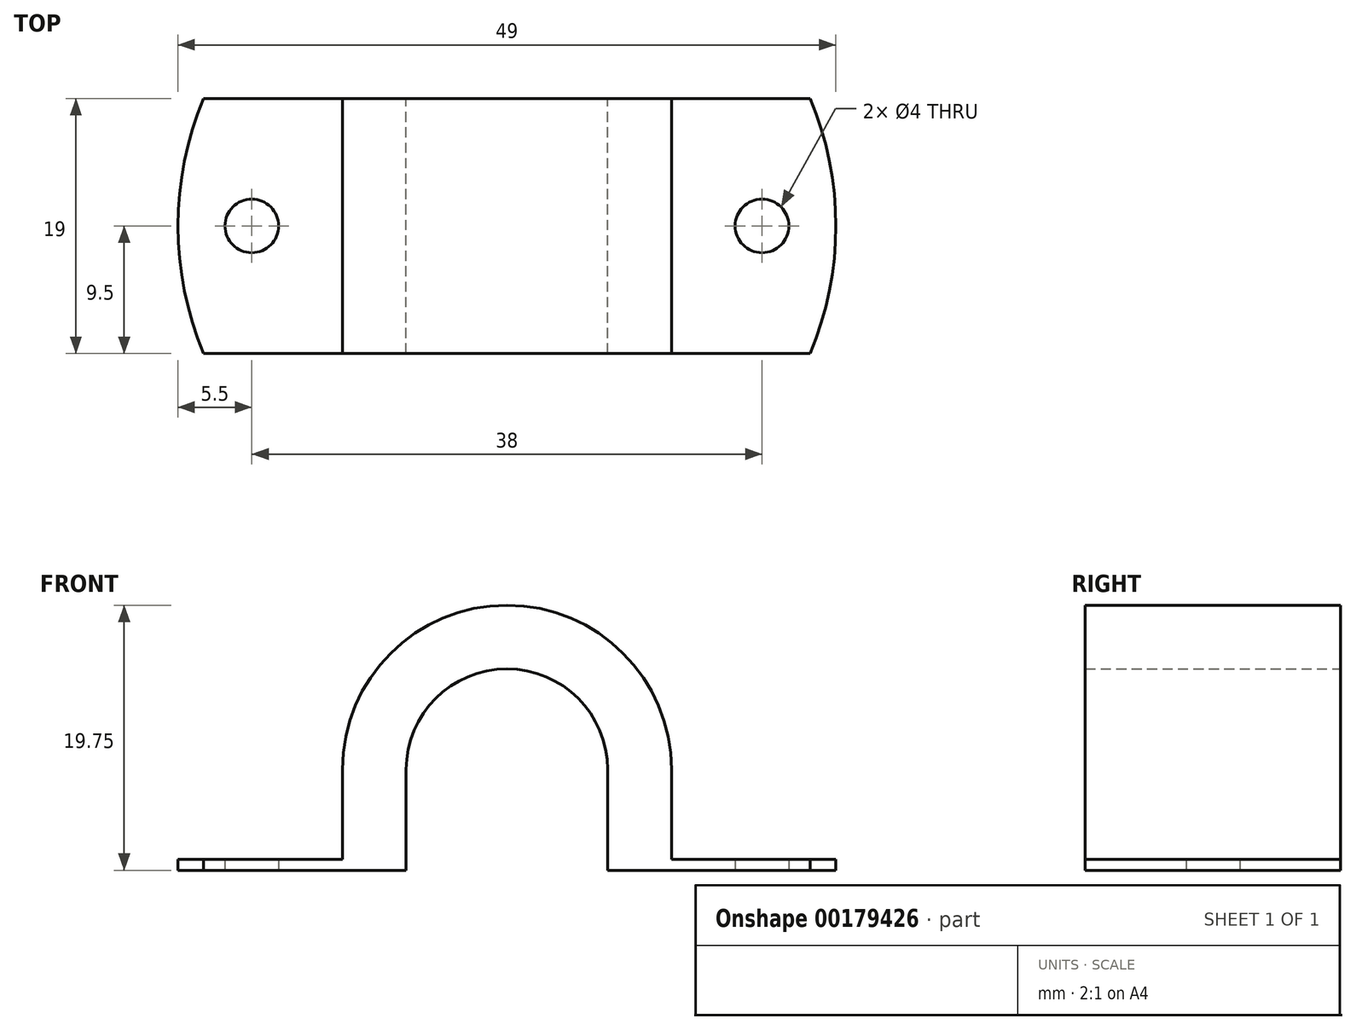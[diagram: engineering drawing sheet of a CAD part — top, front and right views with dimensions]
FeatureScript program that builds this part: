
annotation { "Feature Type Name" : "Feature", "Feature Type Description" : "" }
export const myFeature = defineFeature(function(context is Context, id is Id, definition is map)
    precondition{}
    {
        {
            var Q0;
            Q0=qCreatedBy(makeId("Front.planeOp"),FACE);
            var sketch = newSketch(context, id + "F0", { "sketchPlane" : qUnion([Q0])});
            skLineSegment(sketch, "E0", {"start": v(0, 21.46) * mm, "end": v(0, -15.22) * mm, "construction": true});
            skArc(sketch, "E1", {"start": v(7.5, 7.5) * mm, "mid": v(0, 15) * mm, "end": v(-7.5, 7.5) * mm});
            skLineSegment(sketch, "E2", {"start": v(-24.5, 0) * mm, "end": v(-7.5, 0) * mm});
            skArc(sketch, "E3", {"start": v(12.25, 7.5) * mm, "mid": v(0, 19.75) * mm, "end": v(-12.25, 7.5) * mm});
            skLineSegment(sketch, "E4", {"start": v(-12.25, 7.5) * mm, "end": v(-12.25, 0.8) * mm});
            skLineSegment(sketch, "E5", {"start": v(-12.25, 0.8) * mm, "end": v(-24.5, 0.8) * mm});
            skLineSegment(sketch, "E6", {"start": v(-24.5, 0.8) * mm, "end": v(-24.5, 0) * mm});
            skLineSegment(sketch, "E7", {"start": v(-7.5, 7.5) * mm, "end": v(-7.5, 0) * mm});
            skLineSegment(sketch, "E8.MirrorCS", {"start": v(24.5, 0.8) * mm, "end": v(24.5, 0) * mm});
            skLineSegment(sketch, "E9.MirrorCS", {"start": v(12.25, 7.5) * mm, "end": v(12.25, 0.8) * mm});
            skLineSegment(sketch, "E10.MirrorCS", {"start": v(24.5, 0) * mm, "end": v(7.5, 0) * mm});
            skLineSegment(sketch, "E11.MirrorCS", {"start": v(7.5, 7.5) * mm, "end": v(7.5, 0) * mm});
            skLineSegment(sketch, "E12.MirrorCS", {"start": v(12.25, 0.8) * mm, "end": v(24.5, 0.8) * mm});
            skPoint(sketch, "E13.orphan", {"position": v(0, 0) * mm});
            skSolve(sketch);
        }
        {
            var Q0;
            Q0 = qSketchRegion(id + "F0", true);
            extrude(context, id + "F1", {"entities" : qUnion([Q0]), "depth" : 19 * mm});
        }
        {
            var Q0;
            Q0=makeQuery(id+"F1.opExtrude","SWEPT_FACE",FACE,{"disambiguationData":[OSD([sQuery(id+"F0.wireOp",EDGE,"E2")])]});
            var sketch = newSketch(context, id + "F2", { "sketchPlane" : qUnion([Q0])});
            skLineSegment(sketch, "E14", {"start": v(-24.5, 9.5) * mm, "end": v(24.5, 9.5) * mm, "construction": true});
            skCircle(sketch, "E15", {"center": v(-19, 9.5) * mm, "radius": 2 * mm});
            skPoint(sketch, "E16", {"position": v(0, 9.5) * mm});
            skLineSegment(sketch, "E17", {"start": v(0, 19) * mm, "end": v(0, 0) * mm, "construction": true});
            skCircle(sketch, "E18.MirrorC", {"center": v(19, 9.5) * mm, "radius": 2 * mm});
            skArc(sketch, "E19", {"start": v(-22.58, 19) * mm, "mid": v(-24.5, 9.5) * mm, "end": v(-22.58, 0) * mm});
            skPoint(sketch, "E20", {"position": v(-22.58, 19) * mm});
            skPoint(sketch, "E21", {"position": v(-22.58, 0) * mm});
            skPoint(sketch, "E22", {"position": v(22.58, 0) * mm});
            skPoint(sketch, "E23", {"position": v(22.58, 19) * mm});
            skArc(sketch, "E24.trimOffspring", {"start": v(22.58, 0) * mm, "mid": v(24.5, 9.5) * mm, "end": v(22.58, 19) * mm});
            skLineSegment(sketch, "E25", {"start": v(-22.58, 19) * mm, "end": v(-24.5, 19) * mm});
            skLineSegment(sketch, "E26", {"start": v(-24.5, 19) * mm, "end": v(-24.5, 0) * mm});
            skLineSegment(sketch, "E27", {"start": v(-24.5, 0) * mm, "end": v(-22.58, 0) * mm});
            skLineSegment(sketch, "E28", {"start": v(22.58, 19) * mm, "end": v(24.5, 19) * mm});
            skLineSegment(sketch, "E29", {"start": v(24.5, 19) * mm, "end": v(24.5, 0) * mm});
            skLineSegment(sketch, "E30", {"start": v(24.5, 0) * mm, "end": v(22.58, 0) * mm});
            skSolve(sketch);
        }
        {
            var Q0;
            Q0 = qSketchRegion(id + "F2", true);
            extrude(context, id + "F3", {"entities" : qUnion([Q0]), "operationType" : NewBodyOperationType.REMOVE, "oppositeDirection" : true, "depth" : 25 * mm});
        }
    });
